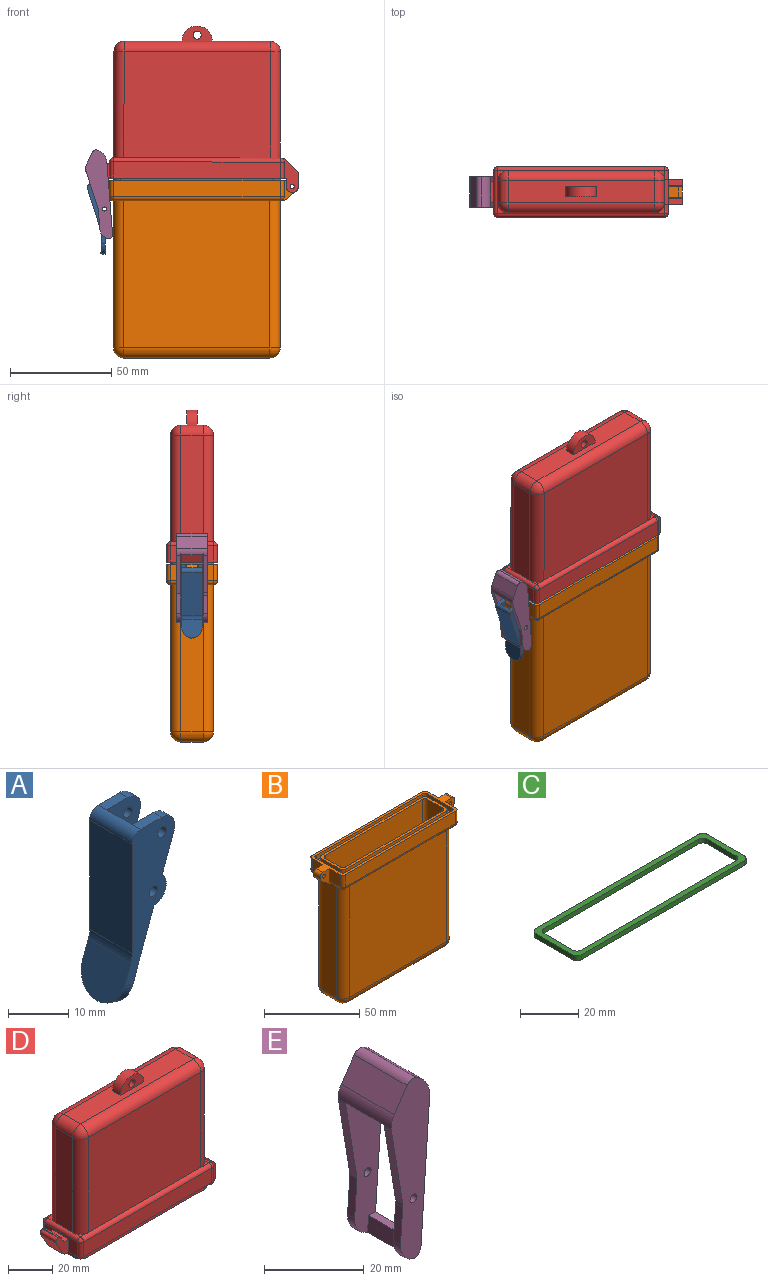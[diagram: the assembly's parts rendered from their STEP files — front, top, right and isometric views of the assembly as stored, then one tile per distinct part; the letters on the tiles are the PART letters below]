
ASSEMBLY  parts=5 mates=5
PART A: 23 faces, bbox 13.4x10x35.2 mm
  f0: plane 5x2mm, normal (0,0,1), area 10mm2, adj f15,f18,f19,f21
  f1: cylinder r=3mm len=5.23mm, axis (0,1,0), area 14.3mm2, adj f2,f8,f10,f11
  f2: plane 7.74x2.82mm, normal (0.94,0,-0.34), area 16.5mm2, adj f1,f3,f10,f11
  f3: cylinder r=3mm len=4.03mm, axis (0,1,0), area 11.5mm2, adj f2,f4,f10,f11
  f4: plane 5x2mm, normal (0,0,1), area 10mm2, adj f3,f10,f11,f21
  f5: plane 22.27x10mm, normal (-1,0,0), area 222.7mm2, adj f10,f18,f21,f22
  f6: plane 10x8.57mm, normal (-0.94,0,0.34), area 80.5mm2, adj f10,f18,f20,f22
  f7: cylinder r=1mm len=2mm, axis (0,1,0), area 12.6mm2, adj f10,f11
  f8: plane 18.24x10mm, normal (0.94,0,-0.34), area 129mm2, adj f1,f10,f11,f12,f13,f18,f19,f20
  f9: cylinder r=1mm len=2mm, axis (0,1,0), area 12.6mm2, adj f10,f11
  f10: plane 30.54x11.71mm, normal (0,-1,0), area 175.7mm2, adj f1,f2,f3,f4,f5,f6,f7,f8
  f11: plane 25.51x8mm, normal (0,1,0), area 115.5mm2, adj f1,f2,f3,f4,f7,f8,f9,f12
  f12: plane 25.51x6mm, normal (1,0,0), area 153.1mm2, adj f8,f11,f19,f21
  f13: cylinder r=3mm len=5.23mm, axis (0,-1,0), area 14.3mm2, adj f8,f14,f18,f19
  f14: plane 7.74x2.82mm, normal (0.94,0,-0.34), area 16.5mm2, adj f13,f15,f18,f19
  f15: cylinder r=3mm len=4.03mm, axis (0,-1,0), area 11.5mm2, adj f0,f14,f18,f19
  f16: cylinder r=1mm len=2mm, axis (0,-1,0), area 12.6mm2, adj f18,f19
  f17: cylinder r=1mm len=2mm, axis (0,-1,0), area 12.6mm2, adj f18,f19
  f18: plane 30.54x11.71mm, normal (0,1,0), area 175.7mm2, adj f0,f5,f6,f8,f13,f14,f15,f16
  f19: plane 25.51x8mm, normal (0,-1,0), area 115.5mm2, adj f0,f8,f12,f13,f14,f15,f16,f17
  f20: cylinder r=5mm len=10mm, axis (-0.94,0,0.34), area 31.4mm2, adj f6,f8,f10,f18
  f21: cylinder r=2mm len=10mm, axis (0,1,0), area 31.4mm2, adj f0,f4,f5,f10,f12,f18
  f22: cylinder r=5mm len=10mm, axis (0,-1,0), area 17.5mm2, adj f5,f6,f10,f18
PART B: 93 faces, bbox 100x25x87.5 mm
  f0: plane 96x25mm, normal (0,0,1), area 374mm2, adj f6,f7,f8,f9,f10,f11,f33,f34
  f1: plane 5x2mm, normal (0,0,-1), area 10mm2, adj f16,f37,f38,f39
  f2: plane 5x2mm, normal (0,0,-1), area 10mm2, adj f14,f30,f33,f34
  f3: plane 5x5mm, normal (0,0,-1), area 5.4mm2, adj f29,f43,f46
  f4: plane 5x5mm, normal (0,0,-1), area 5.4mm2, adj f23,f40,f43
  f5: plane 5x5mm, normal (0,0,-1), area 5.4mm2, adj f18,f48,f50
  f6: plane 8x8mm, normal (-1,0,0), area 64mm2, adj f0,f38,f51,f53
  f7: plane 8x8mm, normal (1,0,0), area 64mm2, adj f0,f33,f47,f48
  f8: plane 8x8mm, normal (-1,0,0), area 64mm2, adj f0,f39,f44,f46
  f9: plane 82x8mm, normal (0,-1,0), area 656mm2, adj f0,f47,f50,f53
  f10: plane 8x8mm, normal (1,0,0), area 64mm2, adj f0,f34,f40,f41
  f11: plane 82x8mm, normal (0,1,0), area 656mm2, adj f0,f41,f43,f44
  f12: plane 5x5mm, normal (0,0,-1), area 5.4mm2, adj f20,f50,f51
  f13: plane 72x11mm, normal (0,0,-1), area 792mm2, adj f21,f22,f26,f27
  f14: plane 72.5x11mm, normal (1,0,0), area 797.5mm2, adj f2,f18,f22,f23,f40,f48
  f15: plane 72.5x72mm, normal (0,-1,0), area 5220mm2, adj f18,f20,f21,f50
  f16: plane 72.5x11mm, normal (-1,0,0), area 797.5mm2, adj f1,f20,f26,f29,f46,f51
  f17: plane 72.5x72mm, normal (0,1,0), area 5220mm2, adj f23,f27,f29,f43
  f18: cylinder r=5mm len=72.5mm, axis (0,0,-1), area 569.4mm2, adj f5,f14,f15,f19
  f19: sphere r=5mm, area 39.3mm2, adj f18,f21,f22
  f20: cylinder r=5mm len=72.5mm, axis (0,0,1), area 569.4mm2, adj f12,f15,f16,f24
  f21: cylinder r=5mm len=72mm, axis (-1,0,0), area 565.5mm2, adj f13,f15,f19,f24
  f22: cylinder r=5mm len=11mm, axis (0,1,0), area 86.4mm2, adj f13,f14,f19,f25
  f23: cylinder r=5mm len=72.5mm, axis (0,0,1), area 569.4mm2, adj f4,f14,f17,f25
  f24: sphere r=5mm, area 39.3mm2, adj f20,f21,f26
  f25: sphere r=5mm, area 39.3mm2, adj f22,f23,f27
  f26: cylinder r=5mm len=11mm, axis (0,-1,0), area 86.4mm2, adj f13,f16,f24,f28
  f27: cylinder r=5mm len=72mm, axis (1,0,0), area 565.5mm2, adj f13,f17,f25,f28
  f28: sphere r=5mm, area 39.3mm2, adj f26,f27,f29
  f29: cylinder r=5mm len=72.5mm, axis (0,0,-1), area 569.4mm2, adj f3,f16,f17,f28
  f30: plane 5.86x5mm, normal (0.62,0,-0.78), area 37.4mm2, adj f2,f31,f33,f34
  f31: cylinder r=3mm len=5mm, axis (0,1,0), area 13.5mm2, adj f30,f32,f33,f34
  f32: plane 5x1mm, normal (1,0,0), area 5mm2, adj f31,f33,f34,f78
  f33: plane 10x9mm, normal (0,-1,0), area 47.1mm2, adj f0,f2,f7,f30,f31,f32,f48,f78
  f34: plane 10x9mm, normal (0,1,0), area 47.1mm2, adj f0,f2,f10,f30,f31,f32,f40,f78
  f35: plane 5x1mm, normal (-1,0,0), area 5mm2, adj f36,f38,f39,f77
  f36: cylinder r=3mm len=5mm, axis (0,1,0), area 13.5mm2, adj f35,f37,f38,f39
  f37: plane 5.86x5mm, normal (-0.62,0,-0.78), area 37.4mm2, adj f1,f36,f38,f39
  f38: plane 10x9mm, normal (0,-1,0), area 47.1mm2, adj f0,f1,f6,f35,f36,f37,f51,f77
  f39: plane 10x9mm, normal (0,1,0), area 47.1mm2, adj f0,f1,f8,f35,f36,f37,f46,f77
  f40: cylinder r=2mm len=8mm, axis (0,1,0), area 25.1mm2, adj f4,f10,f14,f34,f42
  f41: cylinder r=2mm len=8mm, axis (0,0,-1), area 25.1mm2, adj f0,f10,f11,f42
  f42: sphere r=2mm, area 6.3mm2, adj f40,f41,f43
  f43: cylinder r=2mm len=82mm, axis (-1,0,0), area 257.6mm2, adj f3,f4,f11,f17,f42,f45
  f44: cylinder r=2mm len=8mm, axis (0,0,1), area 25.1mm2, adj f0,f8,f11,f45
  f45: sphere r=2mm, area 6.3mm2, adj f43,f44,f46
  f46: cylinder r=2mm len=8mm, axis (0,-1,0), area 25.1mm2, adj f3,f8,f16,f39,f45
  f47: cylinder r=2mm len=8mm, axis (0,0,1), area 25.1mm2, adj f0,f7,f9,f49
  f48: cylinder r=2mm len=8mm, axis (0,1,0), area 25.1mm2, adj f5,f7,f14,f33,f49
  f49: sphere r=2mm, area 6.3mm2, adj f47,f48,f50
  f50: cylinder r=2mm len=82mm, axis (1,0,0), area 257.6mm2, adj f5,f9,f12,f15,f49,f52
  f51: cylinder r=2mm len=8mm, axis (0,-1,0), area 25.1mm2, adj f6,f12,f16,f38,f52
  f52: sphere r=2mm, area 6.3mm2, adj f50,f51,f53
  f53: cylinder r=2mm len=8mm, axis (0,0,-1), area 25.1mm2, adj f0,f6,f9,f52
  f54: plane 18x3mm, normal (-1,0,0), area 54mm2, adj f0,f55,f69,f70
  f55: cylinder r=2mm len=3mm, axis (0,0,1), area 9.4mm2, adj f0,f54,f56,f70
  f56: plane 79x3mm, normal (0,-1,0), area 237mm2, adj f0,f55,f57,f70
  f57: cylinder r=2mm len=3mm, axis (0,0,1), area 9.4mm2, adj f0,f56,f58,f70
  f58: plane 18x3mm, normal (1,0,0), area 54mm2, adj f0,f57,f59,f70
  f59: cylinder r=2mm len=3mm, axis (0,0,1), area 9.4mm2, adj f0,f58,f60,f70
  f60: plane 79x3mm, normal (0,1,0), area 237mm2, adj f0,f59,f69,f70
  f61: cylinder r=2mm len=3mm, axis (0,0,1), area 9.4mm2, adj f62,f68,f70,f76
  f62: plane 75x3mm, normal (0,-1,0), area 225mm2, adj f61,f63,f70,f76
  f63: cylinder r=2mm len=3mm, axis (0,0,1), area 9.4mm2, adj f62,f64,f70,f76
  f64: plane 14x3mm, normal (-1,0,0), area 42mm2, adj f63,f65,f70,f76
  f65: cylinder r=2mm len=3mm, axis (0,0,1), area 9.4mm2, adj f64,f66,f70,f76
  f66: plane 75x3mm, normal (0,1,0), area 225mm2, adj f65,f67,f70,f76
  f67: cylinder r=2mm len=3mm, axis (0,0,1), area 9.4mm2, adj f66,f68,f70,f76
  f68: plane 14x3mm, normal (1,0,0), area 42mm2, adj f61,f67,f70,f76
  f69: cylinder r=2mm len=3mm, axis (0,0,1), area 9.4mm2, adj f0,f54,f60,f70
  f70: plane 83x22mm, normal (0,0,1), area 404mm2, adj f54,f55,f56,f57,f58,f59,f60,f61
  f71: plane 72x11mm, normal (0,0,1), area 792mm2, adj f84,f85,f89,f90
  f72: plane 82.5x72mm, normal (0,-1,0), area 5940mm2, adj f76,f81,f85,f86
  f73: plane 82.5x11mm, normal (1,0,0), area 907.5mm2, adj f76,f81,f83,f84
  f74: plane 82.5x72mm, normal (0,1,0), area 5940mm2, adj f76,f83,f89,f92
  f75: plane 82.5x11mm, normal (-1,0,0), area 907.5mm2, adj f76,f86,f90,f92
  f76: plane 79x18mm, normal (0,0,1), area 282mm2, adj f61,f62,f63,f64,f65,f66,f67,f68
  f77: cylinder r=2mm len=5mm, axis (0,-1,0), area 15.7mm2, adj f0,f35,f38,f39
  f78: cylinder r=2mm len=5mm, axis (0,1,0), area 15.7mm2, adj f0,f32,f33,f34
  f79: cylinder r=1mm len=5mm, axis (0,-1,0), area 31.4mm2, adj f38,f39
  f80: cylinder r=1mm len=5mm, axis (0,-1,0), area 31.4mm2, adj f33,f34
  f81: cylinder r=2mm len=82.5mm, axis (0,0,-1), area 259.2mm2, adj f72,f73,f76,f82
  f82: sphere r=2mm, area 6.3mm2, adj f81,f84,f85
  f83: cylinder r=2mm len=82.5mm, axis (0,0,1), area 259.2mm2, adj f73,f74,f76,f87
  f84: cylinder r=2mm len=11mm, axis (0,-1,0), area 34.6mm2, adj f71,f73,f82,f87
  f85: cylinder r=2mm len=72mm, axis (-1,0,0), area 226.2mm2, adj f71,f72,f82,f88
  f86: cylinder r=2mm len=82.5mm, axis (0,0,1), area 259.2mm2, adj f72,f75,f76,f88
  f87: sphere r=2mm, area 6.3mm2, adj f83,f84,f89
  f88: sphere r=2mm, area 6.3mm2, adj f85,f86,f90
  f89: cylinder r=2mm len=72mm, axis (1,0,0), area 226.2mm2, adj f71,f74,f87,f91
  f90: cylinder r=2mm len=11mm, axis (0,1,0), area 34.6mm2, adj f71,f75,f88,f91
  f91: sphere r=2mm, area 6.3mm2, adj f89,f90,f92
  f92: cylinder r=2mm len=82.5mm, axis (0,0,-1), area 259.2mm2, adj f74,f75,f76,f91
PART C: 18 faces, bbox 83x22x2 mm
  f0: plane 18x2mm, normal (1,0,0), area 36mm2, adj f1,f15,f16,f17
  f1: cylinder r=2mm len=2mm, axis (0,0,-1), area 6.3mm2, adj f0,f2,f16,f17
  f2: plane 79x2mm, normal (0,1,0), area 158mm2, adj f1,f3,f16,f17
  f3: cylinder r=2mm len=2mm, axis (0,0,-1), area 6.3mm2, adj f2,f4,f16,f17
  f4: plane 18x2mm, normal (-1,0,0), area 36mm2, adj f3,f5,f16,f17
  f5: cylinder r=2mm len=2mm, axis (0,0,-1), area 6.3mm2, adj f4,f6,f16,f17
  f6: plane 79x2mm, normal (0,-1,0), area 158mm2, adj f5,f15,f16,f17
  f7: cylinder r=2mm len=2mm, axis (0,0,-1), area 6.3mm2, adj f8,f14,f16,f17
  f8: plane 75x2mm, normal (0,1,0), area 150mm2, adj f7,f9,f16,f17
  f9: cylinder r=2mm len=2mm, axis (0,0,-1), area 6.3mm2, adj f8,f10,f16,f17
  f10: plane 14x2mm, normal (1,0,0), area 28mm2, adj f9,f11,f16,f17
  f11: cylinder r=2mm len=2mm, axis (0,0,-1), area 6.3mm2, adj f10,f12,f16,f17
  f12: plane 75x2mm, normal (0,-1,0), area 150mm2, adj f11,f13,f16,f17
  f13: cylinder r=2mm len=2mm, axis (0,0,-1), area 6.3mm2, adj f12,f14,f16,f17
  f14: plane 14x2mm, normal (-1,0,0), area 28mm2, adj f7,f13,f16,f17
  f15: cylinder r=2mm len=2mm, axis (0,0,-1), area 6.3mm2, adj f0,f6,f16,f17
  f16: plane 83x22mm, normal (0,0,1), area 404mm2, adj f0,f1,f2,f3,f4,f5,f6,f7
  f17: plane 83x22mm, normal (0,0,-1), area 404mm2, adj f0,f1,f2,f3,f4,f5,f6,f7
PART D: 102 faces, bbox 101.2x25x82 mm
  f0: plane 72x11mm, normal (0,0,1), area 717mm2, adj f18,f19,f23,f24,f77,f79,f80
  f1: plane 21x7mm, normal (0,0,1), area 34.7mm2, adj f4,f7,f20,f26,f30,f31,f36,f37
  f2: plane 5x5mm, normal (0,0,1), area 5.4mm2, adj f15,f45,f48
  f3: plane 8x4.5mm, normal (1,0,0), area 36mm2, adj f5,f37,f49,f51
  f4: plane 10x6mm, normal (1,0,0), area 60mm2, adj f1,f5,f32,f38
  f5: plane 89.96x25mm, normal (0,0,-1), area 409.1mm2, adj f3,f4,f11,f12,f13,f14,f27,f31
  f6: plane 72x52.5mm, normal (0,-1,0), area 3780mm2, adj f17,f23,f26,f42
  f7: plane 52.5x11mm, normal (1,0,0), area 577.5mm2, adj f1,f20,f24,f26
  f8: plane 72x52.5mm, normal (0,1,0), area 3780mm2, adj f15,f19,f20,f48
  f9: plane 52.5x11mm, normal (-1,0,0), area 577.5mm2, adj f15,f17,f18,f45
  f10: plane 5x5mm, normal (0,0,1), area 5.4mm2, adj f17,f42,f45
  f11: plane 82x8mm, normal (0,1,0), area 656mm2, adj f5,f46,f48,f49
  f12: plane 8x4.5mm, normal (1,0,0), area 36mm2, adj f5,f31,f39,f40
  f13: plane 82x8mm, normal (0,-1,0), area 656mm2, adj f5,f40,f42,f43
  f14: plane 21x8mm, normal (-1,0,0), area 98mm2, adj f5,f43,f45,f46,f82,f85,f86
  f15: cylinder r=5mm len=52.5mm, axis (0,0,-1), area 412.3mm2, adj f2,f8,f9,f16
  f16: sphere r=5mm, area 39.3mm2, adj f15,f18,f19
  f17: cylinder r=5mm len=52.5mm, axis (0,0,1), area 412.3mm2, adj f6,f9,f10,f21
  f18: cylinder r=5mm len=11mm, axis (0,1,0), area 86.4mm2, adj f0,f9,f16,f21
  f19: cylinder r=5mm len=72mm, axis (-1,0,0), area 565.5mm2, adj f0,f8,f16,f22
  f20: cylinder r=5mm len=52.5mm, axis (0,0,1), area 412.3mm2, adj f1,f7,f8,f22
  f21: sphere r=5mm, area 39.3mm2, adj f17,f18,f23
  f22: sphere r=5mm, area 39.3mm2, adj f19,f20,f24
  f23: cylinder r=5mm len=72mm, axis (1,0,0), area 565.5mm2, adj f0,f6,f21,f25
  f24: cylinder r=5mm len=11mm, axis (0,-1,0), area 86.4mm2, adj f0,f7,f22,f25
  f25: sphere r=5mm, area 39.3mm2, adj f23,f24,f26
  f26: cylinder r=5mm len=52.5mm, axis (0,0,-1), area 412.3mm2, adj f1,f6,f7,f25
  f27: plane 4x3mm, normal (-1,0,0), area 12mm2, adj f5,f28,f31,f32
  f28: cylinder r=3mm len=6mm, axis (0,1,0), area 28.3mm2, adj f27,f29,f31,f32
  f29: plane 7x3mm, normal (1,0,0), area 21mm2, adj f28,f30,f31,f32
  f30: plane 7x7mm, normal (0.71,0,0.71), area 29.7mm2, adj f1,f29,f31,f32
  f31: plane 17x9mm, normal (0,-1,0), area 81.4mm2, adj f1,f5,f12,f27,f28,f29,f30,f39
  f32: plane 17x7mm, normal (0,1,0), area 80.5mm2, adj f4,f5,f27,f28,f29,f30,f76
  f33: plane 4x3mm, normal (-1,0,0), area 12mm2, adj f5,f34,f37,f38
  f34: cylinder r=3mm len=6mm, axis (0,-1,0), area 28.3mm2, adj f33,f35,f37,f38
  f35: plane 7x3mm, normal (1,0,0), area 21mm2, adj f34,f36,f37,f38
  f36: plane 7x7mm, normal (0.71,0,0.71), area 29.7mm2, adj f1,f35,f37,f38
  f37: plane 17x9mm, normal (0,1,0), area 81.4mm2, adj f1,f3,f5,f33,f34,f35,f36,f51
  f38: plane 17x7mm, normal (0,-1,0), area 80.5mm2, adj f4,f5,f33,f34,f35,f36,f75
  f39: cylinder r=2mm len=4.5mm, axis (0,-1,0), area 14.1mm2, adj f1,f12,f31,f41
  f40: cylinder r=2mm len=8mm, axis (0,0,1), area 25.1mm2, adj f5,f12,f13,f41
  f41: sphere r=2mm, area 6.3mm2, adj f39,f40,f42
  f42: cylinder r=2mm len=82mm, axis (-1,0,0), area 257.6mm2, adj f1,f6,f10,f13,f41,f44
  f43: cylinder r=2mm len=8mm, axis (0,0,-1), area 25.1mm2, adj f5,f13,f14,f44
  f44: sphere r=2mm, area 6.3mm2, adj f42,f43,f45
  f45: cylinder r=2mm len=21mm, axis (0,1,0), area 66mm2, adj f2,f9,f10,f14,f44,f47
  f46: cylinder r=2mm len=8mm, axis (0,0,1), area 25.1mm2, adj f5,f11,f14,f47
  f47: sphere r=2mm, area 6.3mm2, adj f45,f46,f48
  f48: cylinder r=2mm len=82mm, axis (1,0,0), area 257.6mm2, adj f1,f2,f8,f11,f47,f50
  f49: cylinder r=2mm len=8mm, axis (0,0,-1), area 25.1mm2, adj f3,f5,f11,f50
  f50: sphere r=2mm, area 6.3mm2, adj f48,f49,f51
  f51: cylinder r=2mm len=4.5mm, axis (0,-1,0), area 14.1mm2, adj f1,f3,f37,f50
  f52: plane 14.4x3mm, normal (-1,0,0), area 43.2mm2, adj f5,f53,f67,f68
  f53: cylinder r=3.6mm len=3.6mm, axis (0,0,1), area 17mm2, adj f5,f52,f54,f68
  f54: plane 75.4x3mm, normal (0,1,0), area 226.2mm2, adj f5,f53,f55,f68
  f55: cylinder r=3.6mm len=3.6mm, axis (0,0,1), area 17mm2, adj f5,f54,f56,f68
  f56: plane 14.4x3mm, normal (1,0,0), area 43.2mm2, adj f5,f55,f57,f68
  f57: cylinder r=3.6mm len=3.6mm, axis (0,0,1), area 17mm2, adj f5,f56,f58,f68
  f58: plane 75.4x3mm, normal (0,-1,0), area 226.2mm2, adj f5,f57,f67,f68
  f59: cylinder r=2mm len=3mm, axis (0,0,1), area 9.4mm2, adj f60,f66,f68,f74
  f60: plane 75.4x3mm, normal (0,-1,0), area 226.2mm2, adj f59,f61,f68,f74
  f61: cylinder r=2mm len=3mm, axis (0,0,1), area 9.4mm2, adj f60,f62,f68,f74
  f62: plane 14.4x3mm, normal (1,0,0), area 43.2mm2, adj f61,f63,f68,f74
  f63: cylinder r=2mm len=3mm, axis (0,0,1), area 9.4mm2, adj f62,f64,f68,f74
  f64: plane 75.4x3mm, normal (0,1,0), area 226.2mm2, adj f63,f65,f68,f74
  f65: cylinder r=2mm len=3mm, axis (0,0,1), area 9.4mm2, adj f64,f66,f68,f74
  f66: plane 14.4x3mm, normal (-1,0,0), area 43.2mm2, adj f59,f65,f68,f74
  f67: cylinder r=3.6mm len=3.6mm, axis (0,0,1), area 17mm2, adj f5,f52,f58,f68
  f68: plane 82.6x21.6mm, normal (0,0,-1), area 315.5mm2, adj f52,f53,f54,f55,f56,f57,f58,f59
  f69: plane 72x11mm, normal (0,0,-1), area 792mm2, adj f92,f93,f97,f98
  f70: plane 72x62.5mm, normal (0,1,0), area 4500mm2, adj f74,f91,f97,f100
  f71: plane 62.5x11mm, normal (1,0,0), area 687.5mm2, adj f74,f94,f98,f100
  f72: plane 72x62.5mm, normal (0,-1,0), area 4500mm2, adj f74,f89,f93,f94
  f73: plane 62.5x11mm, normal (-1,0,0), area 687.5mm2, adj f74,f89,f91,f92
  f74: plane 79.4x18.4mm, normal (0,0,-1), area 321mm2, adj f59,f60,f61,f62,f63,f64,f65,f66
  f75: cylinder r=1mm len=3mm, axis (0,-1,0), area 18.8mm2, adj f37,f38
  f76: cylinder r=1mm len=3mm, axis (0,-1,0), area 18.8mm2, adj f31,f32
  f77: cylinder r=7.5mm len=15mm, axis (0,1,0), area 117.8mm2, adj f0,f79,f80
  f78: cylinder r=2mm len=5mm, axis (0,1,0), area 62.8mm2, adj f79,f80
  f79: plane 15x7.5mm, normal (0,-1,0), area 75.8mm2, adj f0,f77,f78
  f80: plane 15x7.5mm, normal (0,1,0), area 75.8mm2, adj f0,f77,f78
  f81: plane 10x8.75mm, normal (-0.87,0,-0.5), area 101mm2, adj f5,f85,f86,f88
  f82: plane 10x2.42mm, normal (0,0,1), area 24.2mm2, adj f14,f85,f86,f101
  f83: plane 10x2.75mm, normal (0.87,0,0.5), area 31.8mm2, adj f85,f86,f87,f101
  f84: plane 10x0.54mm, normal (0,0,1), area 5.4mm2, adj f85,f86,f87,f88
  f85: plane 11x8.21mm, normal (0,-1,0), area 49.2mm2, adj f5,f14,f81,f82,f83,f84,f87,f88
  f86: plane 11x8.21mm, normal (0,1,0), area 49.2mm2, adj f5,f14,f81,f82,f83,f84,f87,f88
  f87: cylinder r=1.5mm len=10mm, axis (0,1,0), area 15.7mm2, adj f83,f84,f85,f86
  f88: cylinder r=1.5mm len=10mm, axis (0,1,0), area 31.4mm2, adj f81,f84,f85,f86
  f89: cylinder r=2mm len=62.5mm, axis (0,0,1), area 196.3mm2, adj f72,f73,f74,f90
  f90: sphere r=2mm, area 6.3mm2, adj f89,f92,f93
  f91: cylinder r=2mm len=62.5mm, axis (0,0,-1), area 196.3mm2, adj f70,f73,f74,f95
  f92: cylinder r=2mm len=11mm, axis (0,-1,0), area 34.6mm2, adj f69,f73,f90,f95
  f93: cylinder r=2mm len=72mm, axis (1,0,0), area 226.2mm2, adj f69,f72,f90,f96
  f94: cylinder r=2mm len=62.5mm, axis (0,0,-1), area 196.3mm2, adj f71,f72,f74,f96
  f95: sphere r=2mm, area 6.3mm2, adj f91,f92,f97
  f96: sphere r=2mm, area 6.3mm2, adj f93,f94,f98
  f97: cylinder r=2mm len=72mm, axis (-1,0,0), area 226.2mm2, adj f69,f70,f95,f99
  f98: cylinder r=2mm len=11mm, axis (0,1,0), area 34.6mm2, adj f69,f71,f96,f99
  f99: sphere r=2mm, area 6.3mm2, adj f97,f98,f100
  f100: cylinder r=2mm len=62.5mm, axis (0,0,1), area 196.3mm2, adj f70,f71,f74,f99
  f101: cylinder r=1mm len=10mm, axis (0,-1,0), area 10.5mm2, adj f82,f83,f85,f86
PART E: 24 faces, bbox 10.9x15x44.2 mm
  f0: plane 19.02x3.12mm, normal (-0.99,0,-0.16), area 38.6mm2, adj f12,f15,f21,f23
  f1: plane 42.6x10.85mm, normal (0,-1,0), area 288mm2, adj f2,f5,f6,f7,f9,f10,f11,f16
  f2: plane 35.92x15mm, normal (1,0,-0.07), area 167.5mm2, adj f1,f3,f8,f9,f12,f15,f16,f18
  f3: cylinder r=7mm len=15mm, axis (0,-1,0), area 115.7mm2, adj f2,f8,f15,f19
  f4: plane 15x5.38mm, normal (-0.83,0,0.56), area 97.3mm2, adj f8,f15,f19,f21
  f5: plane 19.59x3.21mm, normal (-0.99,0,-0.16), area 39.7mm2, adj f1,f6,f8,f21
  f6: plane 9.61x2mm, normal (-1,0,0.07), area 19.3mm2, adj f1,f5,f8,f20
  f7: cylinder r=1mm len=2mm, axis (0,-1,0), area 12.6mm2, adj f1,f8
  f8: plane 44.24x10.87mm, normal (0,1,0), area 321.6mm2, adj f2,f3,f4,f5,f6,f7,f18,f19
  f9: cylinder r=1mm len=11mm, axis (0,-1,0), area 33.1mm2, adj f1,f2,f11,f12
  f10: plane 11x7.7mm, normal (0.83,0,-0.56), area 102.1mm2, adj f1,f11,f12,f21
  f11: cylinder r=5mm len=11mm, axis (0,-1,0), area 71.7mm2, adj f1,f9,f10,f12
  f12: plane 42.6x10.85mm, normal (0,1,0), area 288.1mm2, adj f0,f2,f9,f10,f11,f13,f14,f16
  f13: plane 9.03x2mm, normal (-1,0,0.07), area 18.1mm2, adj f12,f15,f22,f23
  f14: cylinder r=1mm len=2mm, axis (0,1,0), area 12.6mm2, adj f12,f15
  f15: plane 44.24x10.87mm, normal (0,-1,0), area 321.6mm2, adj f0,f2,f3,f4,f13,f14,f18,f19
  f16: plane 11x2mm, normal (0.07,0,1), area 22mm2, adj f1,f2,f12,f17
  f17: plane 11x3.99mm, normal (-1,0,0.07), area 44mm2, adj f1,f12,f16,f18
  f18: cylinder r=2mm len=15mm, axis (0,-1,0), area 47.1mm2, adj f2,f8,f15,f17,f20,f22
  f19: cylinder r=2mm len=15mm, axis (0,-1,0), area 43.4mm2, adj f3,f4,f8,f15
  f20: cylinder r=5mm len=5.16mm, axis (0,-1,0), area 13.7mm2, adj f1,f6,f8,f18
  f21: cylinder r=5mm len=15mm, axis (0,-1,0), area 50.7mm2, adj f0,f1,f4,f5,f8,f10,f12,f15
  f22: cylinder r=5mm len=5.16mm, axis (0,-1,0), area 13.7mm2, adj f12,f13,f15,f18
  f23: cylinder r=5mm len=2mm, axis (0,1,0), area 2.3mm2, adj f0,f12,f13,f15
PLACE A rot(axis=(0,-1,0),17.8deg) t=(-0.11,0,14.7)mm
PLACE B at identity fixed
PLACE C at identity
PLACE D rot(axis=(0,1,0),0.1deg) t=(-0.01,0,0.1)mm
PLACE E rot(axis=(0,-1,0),8.5deg) t=(2.33,0,7.1)mm
MATE revolute E.f9 <-> D.f101  axis (0,-1,0) through (-45.4,0,19.19)mm
MATE revolute B.f31 <-> D.f28  axis (0,-1,0) through (47,-2.5,7)mm
MATE fastened C.f17 <-> B.f70  axis (0,0,-1) through (0,0,7)mm
MATE revolute B.f36 <-> A.f3  axis (0,1,0) through (-47,2.5,7)mm
MATE revolute E.f7 <-> A.f1  axis (0,1,0) through (-45.54,-5.5,-4.08)mm
